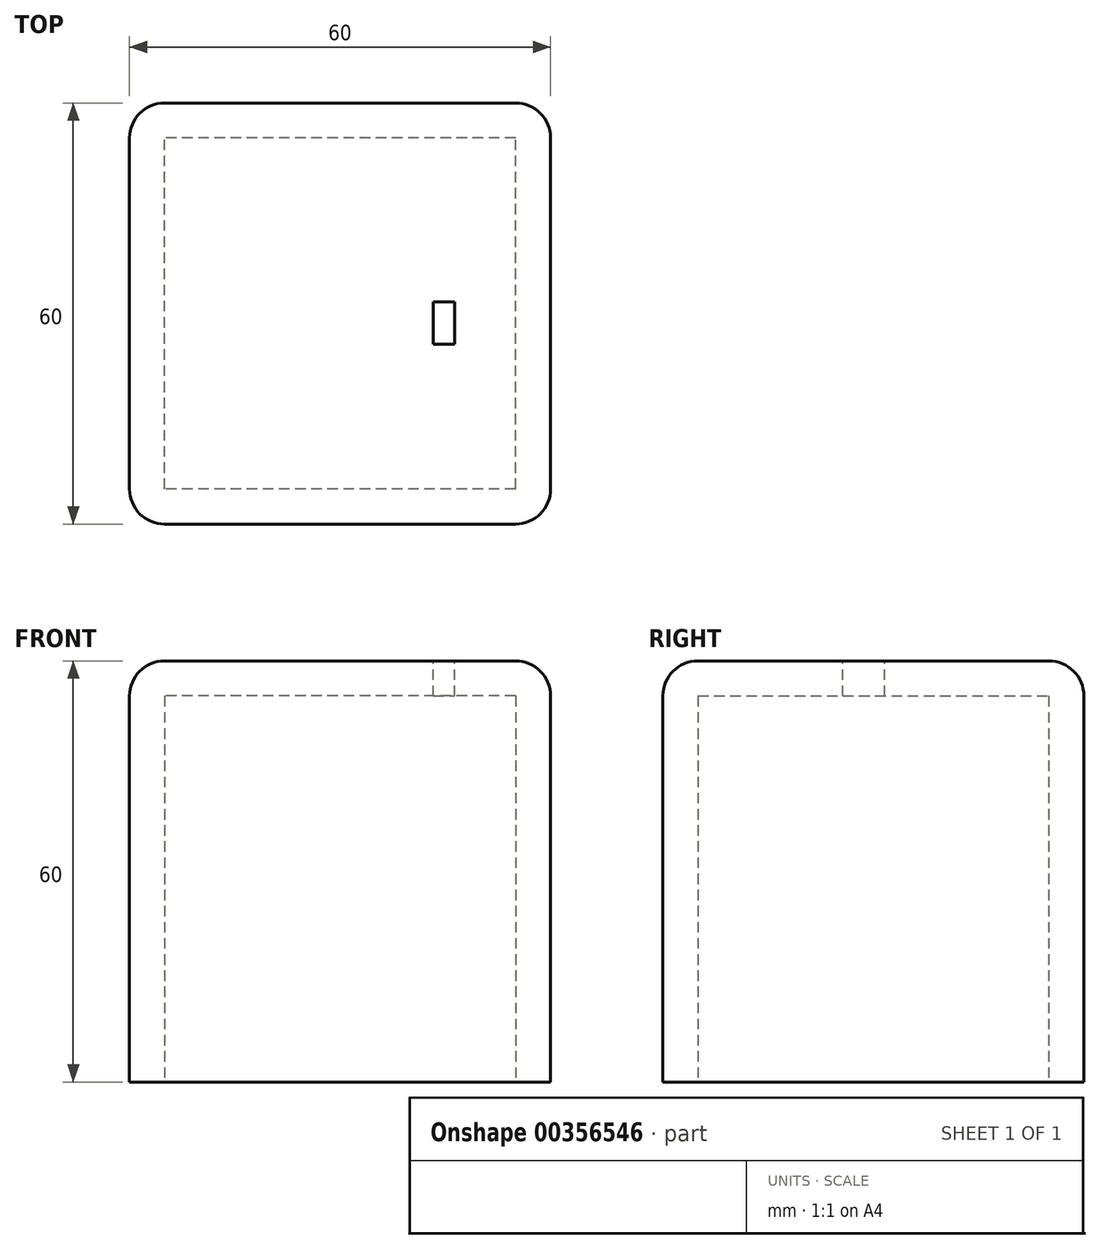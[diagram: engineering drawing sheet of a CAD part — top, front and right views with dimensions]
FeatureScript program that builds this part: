
annotation { "Feature Type Name" : "Feature", "Feature Type Description" : "" }
export const myFeature = defineFeature(function(context is Context, id is Id, definition is map)
    precondition{}
    {
        {
            var Q0;
            Q0=qCreatedBy(makeId("Top.planeOp"),FACE);
            var sketch = newSketch(context, id + "F0", { "sketchPlane" : qUnion([Q0])});
            skLineSegment(sketch, "E0.bottom", {"start": v(-34.4, 28.93) * mm, "end": v(25.6, 28.93) * mm});
            skLineSegment(sketch, "E0.top", {"start": v(-34.4, -31.07) * mm, "end": v(25.6, -31.07) * mm});
            skLineSegment(sketch, "E0.left", {"start": v(-34.4, 28.93) * mm, "end": v(-34.4, -31.07) * mm});
            skLineSegment(sketch, "E0.right", {"start": v(25.6, 28.93) * mm, "end": v(25.6, -31.07) * mm});
            skSolve(sketch);
        }
        {
            var Q0;
            Q0=makeQuery(id+"F0.imprint","IMPRINT",FACE,{"disambiguationData":[TD([[makeQuery(id+"F0.imprint","IMPRINT",EDGE,{"derivedFrom":sQuery(id+"F0.wireOp",EDGE,"E0.bottom")}),-1.0]])]});
            extrude(context, id + "F1", {"entities" : qUnion([Q0]), "depth" : 60 * mm});
        }
        {
            var Q0;
            Q0=makeQuery(id+"F1.opExtrude","SWEPT_EDGE",EDGE,{"disambiguationData":[OSD([sQuery(id+"F0.wireOp",EDGE,"E0.bottom"),sQuery(id+"F0.wireOp",EDGE,"E0.right")])]});
            var Q1;
            Q1=makeQuery(id+"F1.opExtrude","CAP_EDGE",EDGE,{"disambiguationData":[OSD([sQuery(id+"F0.wireOp",EDGE,"E0.bottom")])],"isStart":false});
            var Q2;
            Q2=makeQuery(id+"F1.opExtrude","SWEPT_EDGE",EDGE,{"disambiguationData":[OSD([sQuery(id+"F0.wireOp",EDGE,"E0.bottom"),sQuery(id+"F0.wireOp",EDGE,"E0.left")])]});
            var Q3;
            Q3=makeQuery(id+"F1.opExtrude","CAP_EDGE",EDGE,{"disambiguationData":[OSD([sQuery(id+"F0.wireOp",EDGE,"E0.left")])],"isStart":false});
            var Q4;
            Q4=makeQuery(id+"F1.opExtrude","SWEPT_EDGE",EDGE,{"disambiguationData":[OSD([sQuery(id+"F0.wireOp",EDGE,"E0.top"),sQuery(id+"F0.wireOp",EDGE,"E0.left")])]});
            var Q5;
            Q5=makeQuery(id+"F1.opExtrude","CAP_EDGE",EDGE,{"disambiguationData":[OSD([sQuery(id+"F0.wireOp",EDGE,"E0.top")])],"isStart":false});
            var Q6;
            Q6=makeQuery(id+"F1.opExtrude","SWEPT_EDGE",EDGE,{"disambiguationData":[OSD([sQuery(id+"F0.wireOp",EDGE,"E0.top"),sQuery(id+"F0.wireOp",EDGE,"E0.right")])]});
            var Q7;
            Q7=makeQuery(id+"F1.opExtrude","CAP_EDGE",EDGE,{"disambiguationData":[OSD([sQuery(id+"F0.wireOp",EDGE,"E0.right")])],"isStart":false});
            fillet(context, id + "F2", {"entities" : qUnion([Q0, Q1, Q2, Q3, Q4, Q5, Q6, Q7]), "radius" : 5 * mm, "tangentPropagation" : true, "allowEdgeOverflow" : false});
        }
        {
            var Q0;
            Q0=makeQuery(id+"F1.opExtrude","CAP_FACE",FACE,{"disambiguationData":[OSD([sQuery(id+"F0.wireOp",EDGE,"E0.bottom"),sQuery(id+"F0.wireOp",EDGE,"E0.top"),sQuery(id+"F0.wireOp",EDGE,"E0.left"),sQuery(id+"F0.wireOp",EDGE,"E0.right")])],"isStart":true});
            shell(context, id + "F3", {"entities" : qUnion([Q0]), "thickness" : 5 * mm});
        }
        {
            var Q0;
            Q0=makeQuery(id+"F1.opExtrude","CAP_FACE",FACE,{"disambiguationData":[OSD([sQuery(id+"F0.wireOp",EDGE,"E0.bottom"),sQuery(id+"F0.wireOp",EDGE,"E0.top"),sQuery(id+"F0.wireOp",EDGE,"E0.left"),sQuery(id+"F0.wireOp",EDGE,"E0.right")])],"isStart":false});
            var sketch = newSketch(context, id + "F4", { "sketchPlane" : qUnion([Q0])});
            skLineSegment(sketch, "E1.bottom", {"start": v(8.9, -5.43) * mm, "end": v(11.9, -5.43) * mm});
            skLineSegment(sketch, "E1.top", {"start": v(8.9, 0.57) * mm, "end": v(11.9, 0.57) * mm});
            skLineSegment(sketch, "E1.left", {"start": v(8.9, -5.43) * mm, "end": v(8.9, 0.57) * mm});
            skLineSegment(sketch, "E1.right", {"start": v(11.9, -5.43) * mm, "end": v(11.9, 0.57) * mm});
            skSolve(sketch);
        }
        {
            var Q0;
            Q0=makeQuery(id+"F4.imprint","IMPRINT",FACE,{"disambiguationData":[TD([[makeQuery(id+"F4.imprint","IMPRINT",EDGE,{"derivedFrom":sQuery(id+"F4.wireOp",EDGE,"E1.bottom")}),1.0]])]});
            extrude(context, id + "F5", {"entities" : qUnion([Q0]), "operationType" : NewBodyOperationType.REMOVE, "oppositeDirection" : true, "depth" : 25 * mm});
        }
    });
